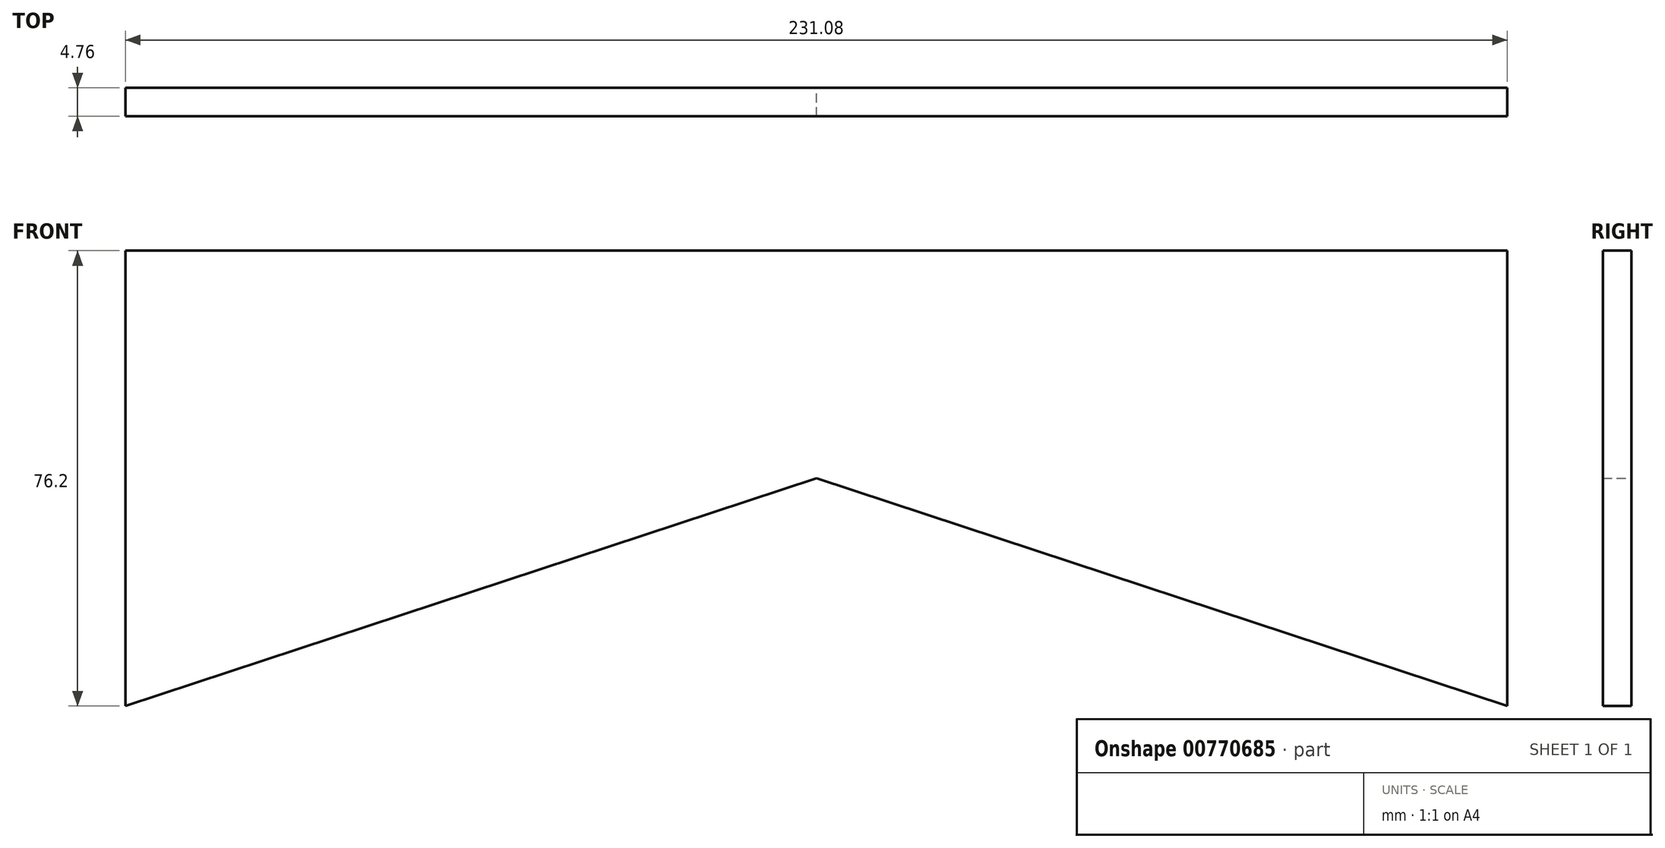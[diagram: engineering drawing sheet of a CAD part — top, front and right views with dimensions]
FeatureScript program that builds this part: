
annotation { "Feature Type Name" : "Feature", "Feature Type Description" : "" }
export const myFeature = defineFeature(function(context is Context, id is Id, definition is map)
    precondition{}
    {
        {
            var Q0;
            Q0=qCreatedBy(makeId("Front.planeOp"),FACE);
            var sketch = newSketch(context, id + "F0", { "sketchPlane" : qUnion([Q0])});
            skLineSegment(sketch, "E0.top", {"start": v(115.54, 38.1) * mm, "end": v(-115.54, 38.1) * mm});
            skLineSegment(sketch, "E0.left", {"start": v(115.54, -38.1) * mm, "end": v(115.54, 38.1) * mm});
            skLineSegment(sketch, "E0.right", {"start": v(-115.54, -38.1) * mm, "end": v(-115.54, 38.1) * mm});
            skPoint(sketch, "E0.middle", {"position": v(0, 0) * mm});
            skLineSegment(sketch, "E1", {"start": v(0, 0) * mm, "end": v(-115.54, -38.1) * mm});
            skLineSegment(sketch, "E2", {"start": v(115.54, -38.1) * mm, "end": v(0, 0) * mm});
            skSolve(sketch);
        }
        {
            var Q0;
            Q0=makeQuery(id+"F0.imprint","IMPRINT",FACE,{"disambiguationData":[TD([[makeQuery(id+"F0.imprint","IMPRINT",EDGE,{"derivedFrom":sQuery(id+"F0.wireOp",EDGE,"E0.top")}),1.0]])]});
            extrude(context, id + "F1", {"entities" : qUnion([Q0]), "endBound" : BoundingType.SYMMETRIC, "depth" : 4.76 * mm, "offsetDistance" : 25.4 * mm});
        }
    });
